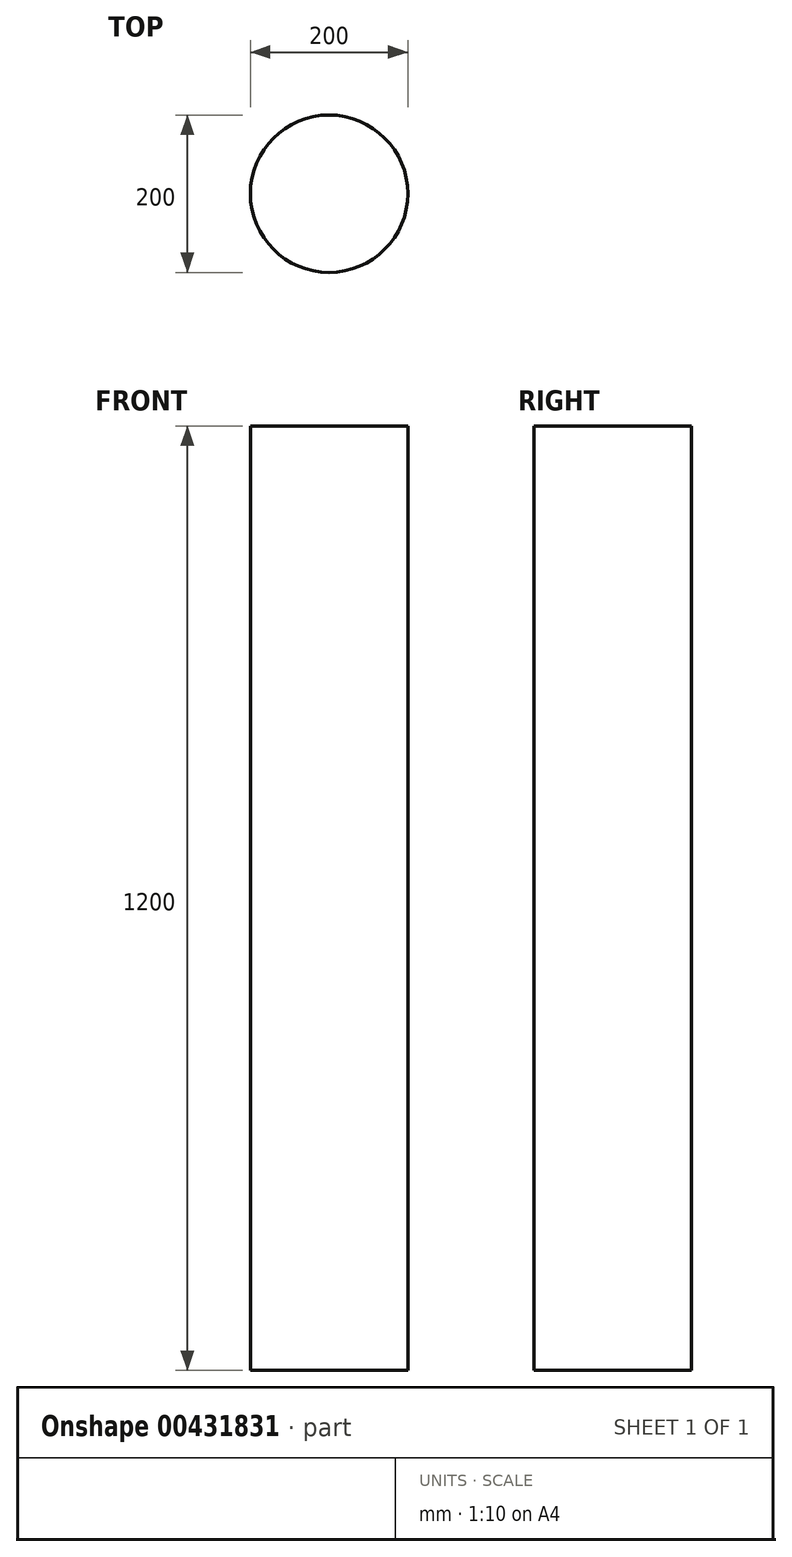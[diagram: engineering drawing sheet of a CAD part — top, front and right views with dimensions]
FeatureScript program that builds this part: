
annotation { "Feature Type Name" : "Feature", "Feature Type Description" : "" }
export const myFeature = defineFeature(function(context is Context, id is Id, definition is map)
    precondition{}
    {
        {
            var Q0;
            Q0=qCreatedBy(makeId("Top.planeOp"),FACE);
            var sketch = newSketch(context, id + "F0", { "sketchPlane" : qUnion([Q0])});
            skCircle(sketch, "E0", {"center": v(0, 0) * mm, "radius": 100 * mm});
            skSolve(sketch);
        }
        {
            var Q0;
            Q0 = qSketchRegion(id + "F0", true);
            extrude(context, id + "F1", {"entities" : qUnion([Q0]), "depth" : 1200 * mm, "offsetDistance" : 25 * mm});
        }
    });
